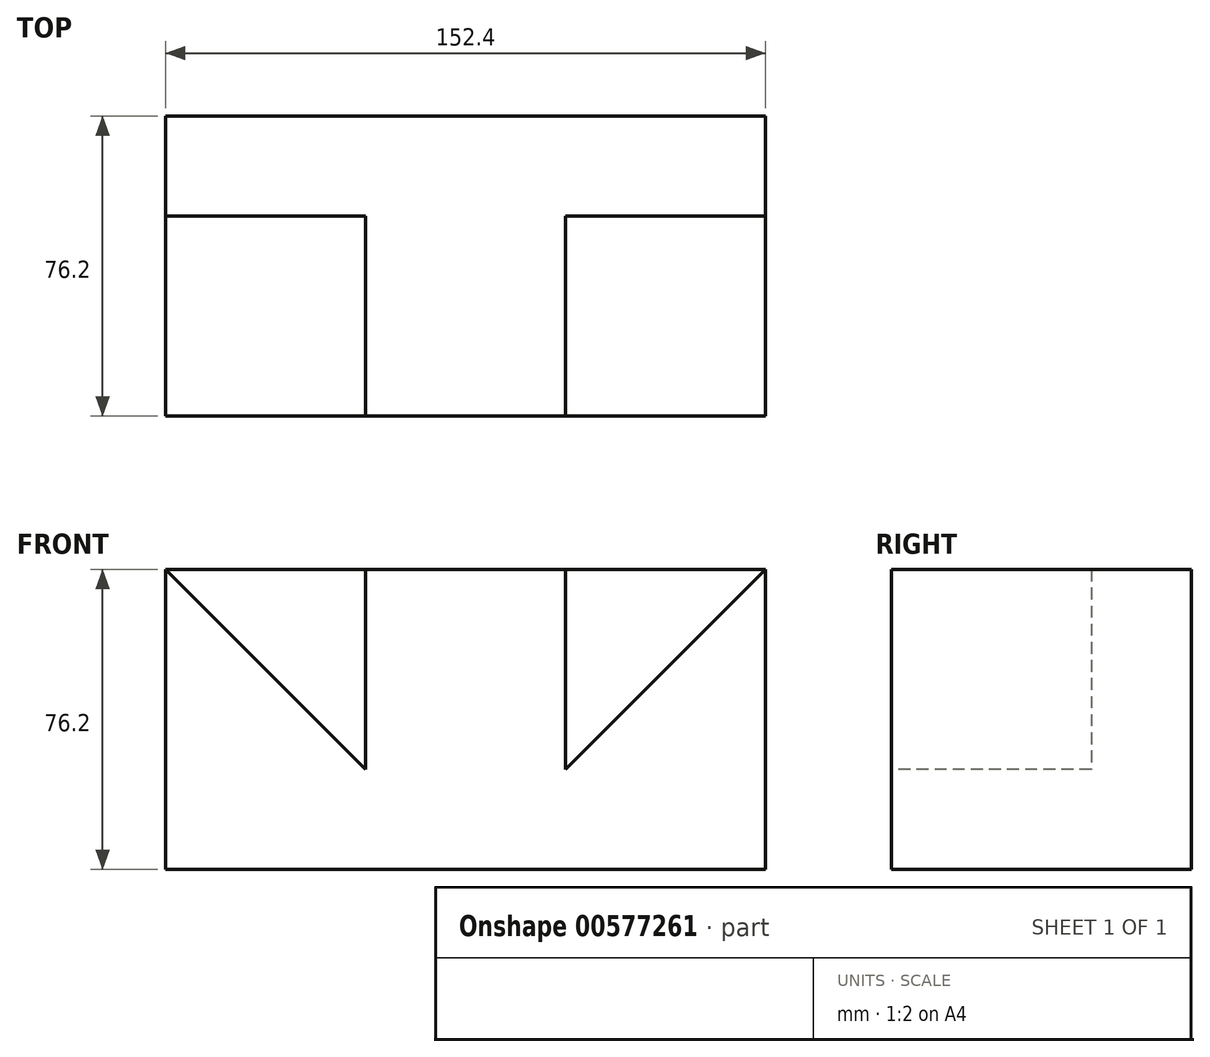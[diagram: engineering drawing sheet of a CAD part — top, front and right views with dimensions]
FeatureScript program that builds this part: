
annotation { "Feature Type Name" : "Feature", "Feature Type Description" : "" }
export const myFeature = defineFeature(function(context is Context, id is Id, definition is map)
    precondition{}
    {
        {
            var Q0;
            Q0=qCreatedBy(makeId("Top.planeOp"),FACE);
            var sketch = newSketch(context, id + "F0", { "sketchPlane" : qUnion([Q0])});
            skLineSegment(sketch, "E0.bottom", {"start": v(-74.54, 2.76) * mm, "end": v(77.86, 2.76) * mm});
            skLineSegment(sketch, "E0.top", {"start": v(-74.54, -73.44) * mm, "end": v(77.86, -73.44) * mm});
            skLineSegment(sketch, "E0.left", {"start": v(-74.54, 2.76) * mm, "end": v(-74.54, -73.44) * mm});
            skLineSegment(sketch, "E0.right", {"start": v(77.86, 2.76) * mm, "end": v(77.86, -73.44) * mm});
            skSolve(sketch);
        }
        {
            var Q0;
            Q0 = qSketchRegion(id + "F0", true);
            extrude(context, id + "F1", {"entities" : qUnion([Q0]), "depth" : 101.6 * mm, "offsetDistance" : 25.4 * mm});
        }
        {
            var Q0;
            Q0=makeQuery(id+"F1.opExtrude","SWEPT_FACE",FACE,{"disambiguationData":[OSD([sQuery(id+"F0.wireOp",EDGE,"E0.right")])]});
            var sketch = newSketch(context, id + "F2", { "sketchPlane" : qUnion([Q0])});
            skLineSegment(sketch, "E1.bottom", {"start": v(-73.44, 0) * mm, "end": v(2.76, 0) * mm});
            skLineSegment(sketch, "E1.top", {"start": v(-73.44, 76.2) * mm, "end": v(2.76, 76.2) * mm});
            skLineSegment(sketch, "E1.left", {"start": v(-73.44, 0) * mm, "end": v(-73.44, 76.2) * mm});
            skLineSegment(sketch, "E1.right", {"start": v(2.76, 0) * mm, "end": v(2.76, 76.2) * mm});
            skLineSegment(sketch, "E2.bottom", {"start": v(2.76, 101.6) * mm, "end": v(-22.64, 101.6) * mm});
            skLineSegment(sketch, "E2.top", {"start": v(2.76, 76.2) * mm, "end": v(-22.64, 76.2) * mm});
            skLineSegment(sketch, "E2.left", {"start": v(2.76, 101.6) * mm, "end": v(2.76, 76.2) * mm});
            skLineSegment(sketch, "E2.right", {"start": v(-22.64, 101.6) * mm, "end": v(-22.64, 76.2) * mm});
            skSolve(sketch);
        }
        {
            var Q0;
            {var subQ0=sQuery(id+"F2.wireOp",EDGE,"E1.top");Q0=makeQuery(id+"F2.imprint","IMPRINT",FACE,{"disambiguationData":[TD([[makeQuery(id+"F2.imprint","IMPRINT",EDGE,{"derivedFrom":subQ0}),1.0]])]});}
            extrude(context, id + "F3", {"entities" : qUnion([Q0]), "operationType" : NewBodyOperationType.REMOVE, "oppositeDirection" : true, "depth" : 152.4 * mm, "offsetDistance" : 25.4 * mm});
        }
        {
            var Q0;
            Q0=makeQuery(id+"F1.opExtrude","SWEPT_FACE",FACE,{"disambiguationData":[OSD([sQuery(id+"F0.wireOp",EDGE,"E0.top")])]});
            var sketch = newSketch(context, id + "F4", { "sketchPlane" : qUnion([Q0])});
            skLineSegment(sketch, "E3.bottom", {"start": v(-74.54, 76.2) * mm, "end": v(-23.74, 76.2) * mm});
            skLineSegment(sketch, "E3.top", {"start": v(-74.54, 0) * mm, "end": v(-23.74, 0) * mm});
            skLineSegment(sketch, "E3.left", {"start": v(-74.54, 76.2) * mm, "end": v(-74.54, 0) * mm});
            skLineSegment(sketch, "E3.right", {"start": v(-23.74, 76.2) * mm, "end": v(-23.74, 0) * mm});
            skLineSegment(sketch, "E4.top", {"start": v(-23.74, 0) * mm, "end": v(27.06, 0) * mm});
            skLineSegment(sketch, "E4.right", {"start": v(27.06, 76.2) * mm, "end": v(27.06, 0) * mm});
            skLineSegment(sketch, "E5.bottom", {"start": v(27.06, 76.2) * mm, "end": v(77.86, 76.2) * mm});
            skLineSegment(sketch, "E5.top", {"start": v(27.06, 0) * mm, "end": v(77.86, 0) * mm});
            skLineSegment(sketch, "E5.right", {"start": v(77.86, 76.2) * mm, "end": v(77.86, 0) * mm});
            skLineSegment(sketch, "E6.left", {"start": v(-23.74, 25.4) * mm, "end": v(-23.74, 0) * mm});
            skLineSegment(sketch, "E6.right", {"start": v(27.06, 41.25) * mm, "end": v(27.06, 0) * mm});
            skLineSegment(sketch, "E7.bottom", {"start": v(-23.74, 25.4) * mm, "end": v(27.06, 25.4) * mm});
            skLineSegment(sketch, "E7.right", {"start": v(27.06, 25.4) * mm, "end": v(27.06, 0) * mm});
            skLineSegment(sketch, "E8", {"start": v(-74.54, 76.2) * mm, "end": v(-23.74, 25.4) * mm});
            skLineSegment(sketch, "E9", {"start": v(27.06, 25.4) * mm, "end": v(77.86, 76.2) * mm});
            skSolve(sketch);
        }
        {
            var Q0;
            Q0=makeQuery(id+"F4.imprint","IMPRINT",FACE,{"disambiguationData":[TD([[makeQuery(id+"F4.imprint","IMPRINT",EDGE,{"derivedFrom":sQuery(id+"F4.wireOp",EDGE,"E5.bottom")}),-1.0]])]});
            var Q1;
            {var subQ1=sQuery(id+"F4.wireOp",EDGE,"E3.right");Q1=makeQuery(id+"F4.imprint","IMPRINT",FACE,{"disambiguationData":[TD([[makeQuery(id+"F4.imprint","IMPRINT",EDGE,{"derivedFrom":subQ1}),1.0]])]});}
            var Q2;
            Q2=makeQuery(id+"F4.imprint","IMPRINT",FACE,{"disambiguationData":[TD([[makeQuery(id+"F4.imprint","IMPRINT",EDGE,{"derivedFrom":sQuery(id+"F4.wireOp",EDGE,"E3.bottom")}),-1.0]])]});
            extrude(context, id + "F5", {"entities" : qUnion([Q0, Q1, Q2]), "operationType" : NewBodyOperationType.REMOVE, "oppositeDirection" : true, "depth" : 50.8 * mm, "offsetDistance" : 25.4 * mm});
        }
    });
